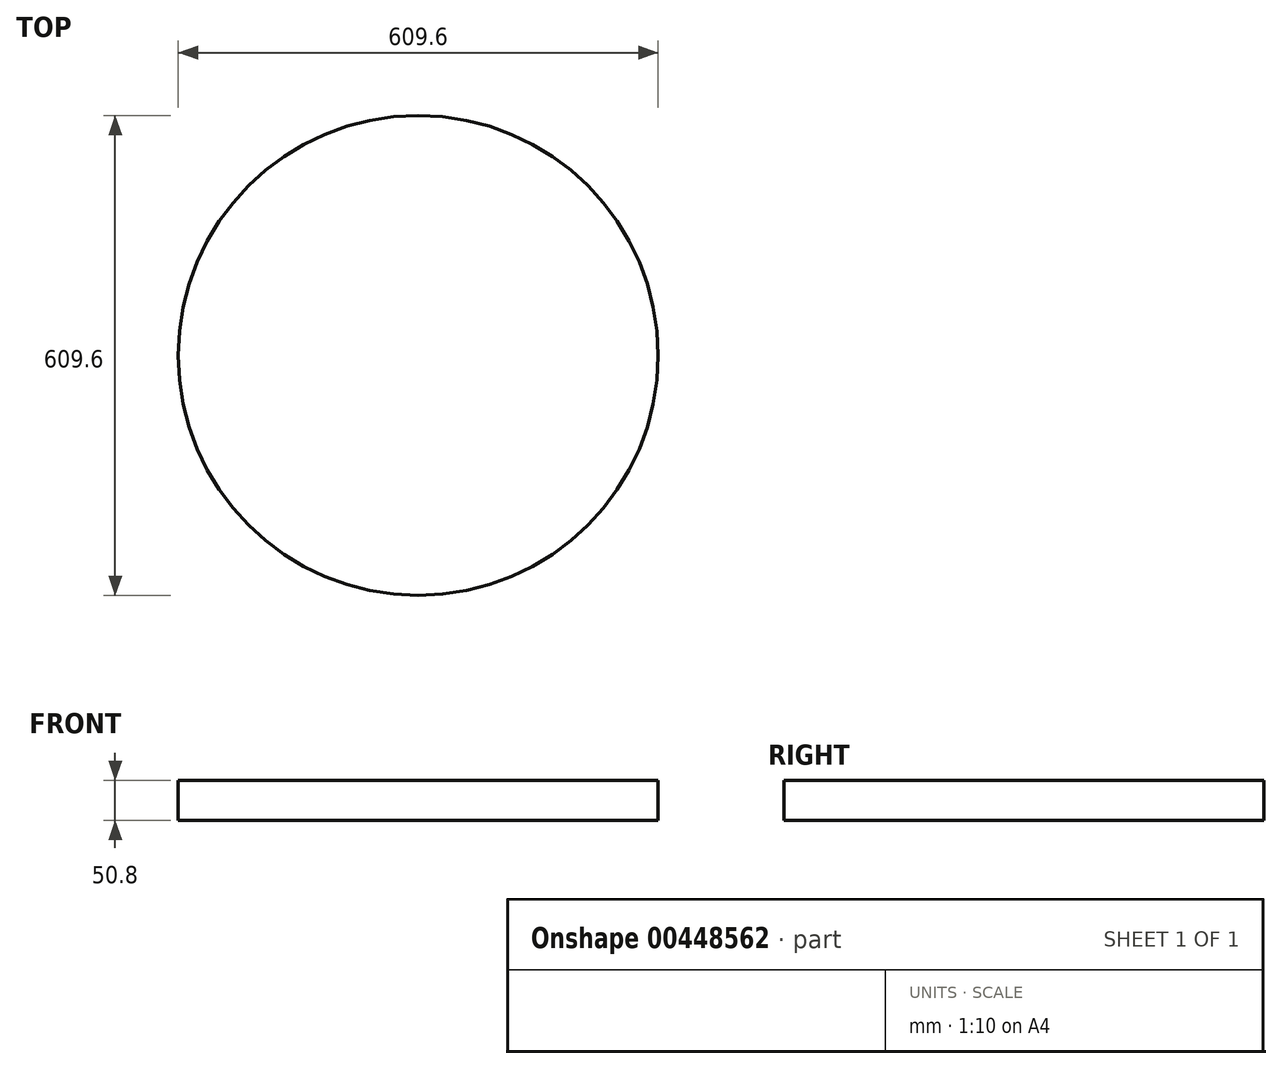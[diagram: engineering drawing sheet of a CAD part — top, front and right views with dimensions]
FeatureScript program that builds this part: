
annotation { "Feature Type Name" : "Feature", "Feature Type Description" : "" }
export const myFeature = defineFeature(function(context is Context, id is Id, definition is map)
    precondition{}
    {
        {
            var Q0;
            Q0=qCreatedBy(makeId("Top.planeOp"),FACE);
            var sketch = newSketch(context, id + "F0", { "sketchPlane" : qUnion([Q0])});
            skLineSegment(sketch, "E0.bottom", {"start": v(304.8, 304.8) * mm, "end": v(-304.8, 304.8) * mm});
            skLineSegment(sketch, "E0.top", {"start": v(304.8, -304.8) * mm, "end": v(-304.8, -304.8) * mm});
            skLineSegment(sketch, "E0.left", {"start": v(304.8, 304.8) * mm, "end": v(304.8, -304.8) * mm});
            skLineSegment(sketch, "E0.right", {"start": v(-304.8, 304.8) * mm, "end": v(-304.8, -304.8) * mm});
            skPoint(sketch, "E0.middle", {"position": v(0, 0) * mm});
            skSolve(sketch);
        }
        {
            var Q0;
            Q0=makeQuery(id+"F0.imprint","IMPRINT",FACE,{"disambiguationData":[TD([[makeQuery(id+"F0.imprint","IMPRINT",EDGE,{"derivedFrom":sQuery(id+"F0.wireOp",EDGE,"E0.bottom")}),1.0]])]});
            extrude(context, id + "F1", {"entities" : qUnion([Q0]), "depth" : 50.8 * mm});
        }
        {
            var Q0;
            Q0=makeQuery(id+"F1.opExtrude","CAP_FACE",FACE,{"disambiguationData":[OSD([sQuery(id+"F0.wireOp",EDGE,"E0.bottom"),sQuery(id+"F0.wireOp",EDGE,"E0.top"),sQuery(id+"F0.wireOp",EDGE,"E0.left"),sQuery(id+"F0.wireOp",EDGE,"E0.right")])],"isStart":false});
            var sketch = newSketch(context, id + "F2", { "sketchPlane" : qUnion([Q0])});
            skCircle(sketch, "E1", {"center": v(0, 0) * mm, "radius": 304.8 * mm});
            skSolve(sketch);
        }
        {
            var Q0;
            {var subQ0=sQuery(id+"F2.wireOp",EDGE,"E1");var subQ1=makeQuery(id+"F1.opExtrude","CAP_EDGE",EDGE,{"disambiguationData":[OSD([sQuery(id+"F0.wireOp",EDGE,"E0.bottom")])],"isStart":false});var subQ2=makeQuery(id+"F2.imprint","INTERSECT",VERTEX,{"derivedFrom":[subQ1,subQ0]});Q0=makeQuery(id+"F2.imprint","IMPRINT",FACE,{"disambiguationData":[TD([[makeQuery(id+"F2.imprint","IMPRINT",EDGE,{"disambiguationData":[TD([[subQ2,-1.0]])],"derivedFrom":subQ0}),-1.0]])]});}
            var Q1;
            {var subQ0=sQuery(id+"F2.wireOp",EDGE,"E1");var subQ1=makeQuery(id+"F1.opExtrude","CAP_EDGE",EDGE,{"disambiguationData":[OSD([sQuery(id+"F0.wireOp",EDGE,"E0.bottom")])],"isStart":false});var subQ2=makeQuery(id+"F2.imprint","INTERSECT",VERTEX,{"derivedFrom":[subQ1,subQ0]});Q1=makeQuery(id+"F2.imprint","IMPRINT",FACE,{"disambiguationData":[TD([[makeQuery(id+"F2.imprint","IMPRINT",EDGE,{"disambiguationData":[TD([[subQ2,1.0]])],"derivedFrom":subQ0}),-1.0]])]});}
            var Q2;
            {var subQ0=sQuery(id+"F2.wireOp",EDGE,"E1");var subQ1=makeQuery(id+"F1.opExtrude","CAP_EDGE",EDGE,{"disambiguationData":[OSD([sQuery(id+"F0.wireOp",EDGE,"E0.left")])],"isStart":false});var subQ2=makeQuery(id+"F2.imprint","INTERSECT",VERTEX,{"derivedFrom":[subQ1,subQ0]});Q2=makeQuery(id+"F2.imprint","IMPRINT",FACE,{"disambiguationData":[TD([[makeQuery(id+"F2.imprint","IMPRINT",EDGE,{"disambiguationData":[TD([[subQ2,1.0]])],"derivedFrom":subQ0}),-1.0]])]});}
            var Q3;
            {var subQ0=sQuery(id+"F2.wireOp",EDGE,"E1");var subQ1=makeQuery(id+"F1.opExtrude","CAP_EDGE",EDGE,{"disambiguationData":[OSD([sQuery(id+"F0.wireOp",EDGE,"E0.right")])],"isStart":false});var subQ2=makeQuery(id+"F2.imprint","INTERSECT",VERTEX,{"derivedFrom":[subQ1,subQ0]});Q3=makeQuery(id+"F2.imprint","IMPRINT",FACE,{"disambiguationData":[TD([[makeQuery(id+"F2.imprint","IMPRINT",EDGE,{"disambiguationData":[TD([[subQ2,-1.0]])],"derivedFrom":subQ0}),-1.0]])]});}
            extrude(context, id + "F3", {"entities" : qUnion([Q0, Q1, Q2, Q3]), "operationType" : NewBodyOperationType.REMOVE, "oppositeDirection" : true, "depth" : 50.8 * mm});
        }
    });
